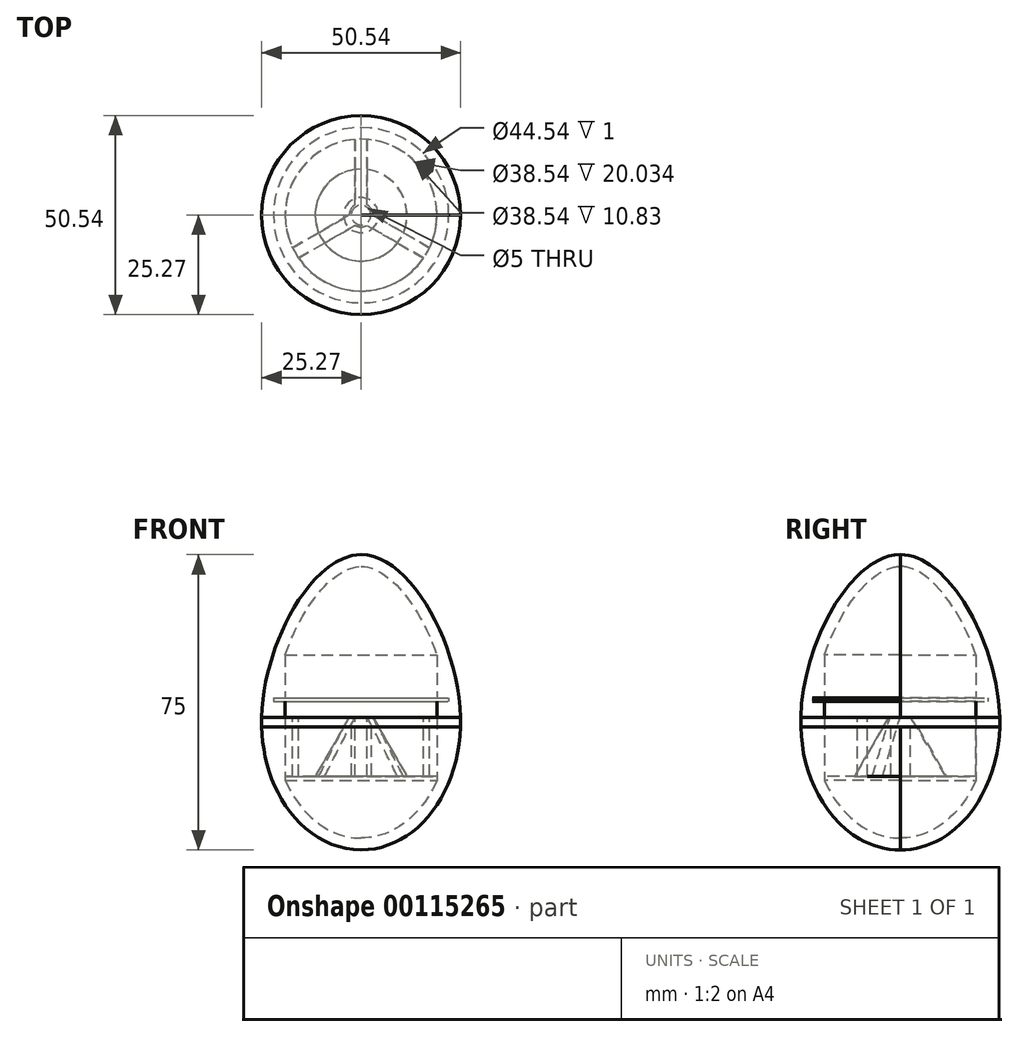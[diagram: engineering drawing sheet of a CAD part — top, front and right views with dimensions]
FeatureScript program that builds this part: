
annotation { "Feature Type Name" : "Feature", "Feature Type Description" : "" }
export const myFeature = defineFeature(function(context is Context, id is Id, definition is map)
    precondition{}
    {
        {
            var Q0;
            Q0=qCreatedBy(makeId("Front.planeOp"),FACE);
            var sketch = newSketch(context, id + "F0", { "sketchPlane" : qUnion([Q0])});
            skFitSpline(sketch, "E0", {"points": [v(0, 41.34) * mm, v(25.28, -2.21) * mm, v(0, -33.66) * mm], "startDerivative": vector(72.85, 0) * mm, "endDerivative": vector(-87.41, 0) * mm});
            skLineSegment(sketch, "E1", {"start": v(0, -33.66) * mm, "end": v(0, 41.34) * mm});
            skLineSegment(sketch, "E2", {"start": v(0, 41.34) * mm, "end": v(-30.8, 41.34) * mm, "construction": true});
            skLineSegment(sketch, "E3", {"start": v(0, -33.66) * mm, "end": v(-29.4, -33.66) * mm, "construction": true});
            skLineSegment(sketch, "E4", {"start": v(25.27, 0) * mm, "end": v(0, 0) * mm});
            skLineSegment(sketch, "E5", {"start": v(0, -33.66) * mm, "end": v(25.27, -33.66) * mm});
            skLineSegment(sketch, "E6", {"start": v(25.27, -33.66) * mm, "end": v(25.27, 41.34) * mm});
            skLineSegment(sketch, "E7", {"start": v(25.27, 41.34) * mm, "end": v(0, 41.34) * mm});
            skSolve(sketch);
        }
        {
            var Q0;
            {var subQ3=sQuery(id+"F0.wireOp",EDGE,"E4");Q0=makeQuery(id+"F0.imprint","IMPRINT",FACE,{"disambiguationData":[TD([[makeQuery(id+"F0.imprint","IMPRINT",EDGE,{"derivedFrom":subQ3}),1.0]])]});}
            var Q1;
            Q1=sQuery(id+"F0.wireOp",EDGE,"E1");
            revolve(context, id + "F1", {"entities" : qUnion([Q0]), "axis" : qUnion([Q1]), "revolveType" : RevolveType.FULL});
        }
        {
            var Q0;
            Q0=makeQuery(id+"F1.opRevolve","SWEPT_FACE",FACE,{"disambiguationData":[OSD([sQuery(id+"F0.wireOp",EDGE,"E4")])]});
            shell(context, id + "F2", {"entities" : qUnion([Q0]), "thickness" : 3 * mm});
        }
        {
            var Q0;
            {var subQ3=sQuery(id+"F0.wireOp",EDGE,"E4");Q0=makeQuery(id+"F0.imprint","IMPRINT",FACE,{"disambiguationData":[TD([[makeQuery(id+"F0.imprint","IMPRINT",EDGE,{"derivedFrom":subQ3}),-1.0]])]});}
            var Q1;
            Q1=sQuery(id+"F0.wireOp",EDGE,"E1");
            revolve(context, id + "F3", {"entities" : qUnion([Q0]), "axis" : qUnion([Q1]), "revolveType" : RevolveType.FULL});
        }
        {
            var Q0;
            Q0=makeQuery(id+"F3.opRevolve","SWEPT_FACE",FACE,{"disambiguationData":[OSD([sQuery(id+"F0.wireOp",EDGE,"E4")])]});
            var sketch = newSketch(context, id + "F4", { "sketchPlane" : qUnion([Q0])});
            skCircle(sketch, "E8", {"center": v(0, 0) * mm, "radius": 22.27 * mm});
            skCircle(sketch, "E9", {"center": v(0, 0) * mm, "radius": 19.27 * mm});
            skSolve(sketch);
        }
        {
            var Q0;
            Q0=makeQuery(id+"F3.opRevolve","SWEPT_FACE",FACE,{"disambiguationData":[OSD([sQuery(id+"F0.wireOp",EDGE,"E4")])]});
            shell(context, id + "F5", {"entities" : qUnion([Q0]), "thickness" : 3 * mm});
        }
        {
            var Q0;
            Q0=makeQuery(id+"F4.imprint","IMPRINT",FACE,{"disambiguationData":[TD([[makeQuery(id+"F4.imprint","IMPRINT",EDGE,{"derivedFrom":sQuery(id+"F4.wireOp",EDGE,"E8")}),1.0]])]});
            var Q1;
            Q1=makeQuery(id+"F4.imprint","IMPRINT",FACE,{"disambiguationData":[TD([[makeQuery(id+"F4.imprint","IMPRINT",EDGE,{"derivedFrom":sQuery(id+"F4.wireOp",EDGE,"E9")}),1.0]])]});
            extrude(context, id + "F6", {"entities" : qUnion([Q0, Q1]), "operationType" : NewBodyOperationType.REMOVE, "oppositeDirection" : true, "depth" : 5 * mm});
        }
        {
            var Q0;
            Q0=makeQuery(id+"F4.imprint","IMPRINT",FACE,{"disambiguationData":[TD([[makeQuery(id+"F4.imprint","IMPRINT",EDGE,{"derivedFrom":sQuery(id+"F4.wireOp",EDGE,"E8")}),1.0]])]});
            extrude(context, id + "F7", {"entities" : qUnion([Q0]), "operationType" : NewBodyOperationType.ADD, "oppositeDirection" : true, "depth" : 4 * mm, "hasSecondDirection" : true, "secondDirectionBound" : SecondDirectionBoundingType.UP_TO_NEXT, "secondDirectionOppositeDirection" : false, "secondDirectionDepth" : 25 * mm});
        }
        {
            var Q0;
            Q0=makeQuery(id+"F6.boolean.opBoolean","COPY",FACE,{"derivedFrom":makeQuery(id+"F6.opExtrude","CAP_FACE",FACE,{"disambiguationData":[OSD([sQuery(id+"F4.wireOp",EDGE,"E8")])],"isStart":false})});
            var sketch = newSketch(context, id + "F8", { "sketchPlane" : qUnion([Q0])});
            skPoint(sketch, "E10", {"position": v(-22.27, 0) * mm});
            skCircle(sketch, "E11", {"center": v(0, 0) * mm, "radius": 19.27 * mm});
            skSolve(sketch);
        }
        {
            var Q0;
            Q0=makeQuery(id+"F8.imprint","IMPRINT",FACE,{"disambiguationData":[TD([[makeQuery(id+"F8.imprint","IMPRINT",EDGE,{"derivedFrom":sQuery(id+"F8.wireOp",EDGE,"E11")}),-1.0]])]});
            extrude(context, id + "F9", {"entities" : qUnion([Q0]), "operationType" : NewBodyOperationType.ADD, "endBound" : BoundingType.UP_TO_NEXT, "oppositeDirection" : true, "depth" : 25 * mm});
        }
        {
            var Q0;
            Q0=qCreatedBy(makeId("Front.planeOp"),FACE);
            var sketch = newSketch(context, id + "F10", { "sketchPlane" : qUnion([Q0])});
            skLineSegment(sketch, "E12", {"start": v(3, 0) * mm, "end": v(19.27, 0) * mm});
            skLineSegment(sketch, "E13", {"start": v(19.27, 0) * mm, "end": v(19.27, -15) * mm});
            skLineSegment(sketch, "E14", {"start": v(19.27, -15) * mm, "end": v(11.66, -15) * mm});
            skLineSegment(sketch, "E15", {"start": v(11.66, -15) * mm, "end": v(3, 0) * mm});
            skLineSegment(sketch, "E16", {"start": v(4.44, -2.5) * mm, "end": v(2.5, -2.5) * mm});
            skLineSegment(sketch, "E17", {"start": v(2.5, -2.5) * mm, "end": v(2.5, -15) * mm});
            skLineSegment(sketch, "E18", {"start": v(2.5, -15) * mm, "end": v(11.66, -15) * mm});
            skLineSegment(sketch, "E19", {"start": v(0, -17.74) * mm, "end": v(0, 5.84) * mm, "construction": true});
            skSolve(sketch);
        }
        {
            var Q0;
            {var subQ2=sQuery(id+"F10.wireOp",EDGE,"E16");Q0=makeQuery(id+"F10.imprint","IMPRINT",FACE,{"disambiguationData":[TD([[makeQuery(id+"F10.imprint","IMPRINT",EDGE,{"derivedFrom":subQ2}),1.0]])]});}
            var Q1;
            Q1=sQuery(id+"F10.wireOp",EDGE,"E19");
            revolve(context, id + "F11", {"entities" : qUnion([Q0]), "axis" : qUnion([Q1]), "revolveType" : RevolveType.FULL});
        }
        {
            var Q0;
            {var subQ3=sQuery(id+"F10.wireOp",EDGE,"E12");Q0=makeQuery(id+"F10.imprint","IMPRINT",FACE,{"disambiguationData":[TD([[makeQuery(id+"F10.imprint","IMPRINT",EDGE,{"derivedFrom":subQ3}),-1.0]])]});}
            var Q1;
            Q1=sQuery(id+"F10.wireOp",EDGE,"E19");
            revolve(context, id + "F12", {"entities" : qUnion([Q0]), "axis" : qUnion([Q1]), "revolveType" : RevolveType.FULL});
        }
        {
            var Q0;
            Q0=makeQuery(id+"F12.opRevolve","SWEPT_FACE",FACE,{"disambiguationData":[OSD([sQuery(id+"F10.wireOp",EDGE,"E12")])]});
            var sketch = newSketch(context, id + "F13", { "sketchPlane" : qUnion([Q0])});
            skLineSegment(sketch, "E20", {"start": v(1.5, 2.6) * mm, "end": v(1.5, 19.21) * mm});
            skLineSegment(sketch, "E21", {"start": v(0, 0) * mm, "end": v(0, 19.27) * mm, "construction": true});
            skLineSegment(sketch, "E22.MirrorCS", {"start": v(-1.5, 2.6) * mm, "end": v(-1.5, 19.21) * mm});
            skArc(sketch, "E23", {"start": v(-1.5, 19.21) * mm, "mid": v(0, 19.27) * mm, "end": v(1.5, 19.21) * mm});
            skArc(sketch, "E24", {"start": v(-1.5, 2.6) * mm, "mid": v(0, 3) * mm, "end": v(1.5, 2.6) * mm});
            skArc(sketch, "E25.1.0", {"start": v(-1.5, -2.6) * mm, "mid": v(-2.6, -1.5) * mm, "end": v(-3, 0) * mm});
            skLineSegment(sketch, "E25.1.1", {"start": v(-1.5, -2.6) * mm, "end": v(-15.89, -10.9) * mm});
            skLineSegment(sketch, "E25.1.2", {"start": v(-3, 0) * mm, "end": v(-17.39, -8.3) * mm});
            skArc(sketch, "E25.1.3", {"start": v(-15.89, -10.9) * mm, "mid": v(-16.69, -9.64) * mm, "end": v(-17.39, -8.3) * mm});
            skArc(sketch, "E25.2.0", {"start": v(3, 0) * mm, "mid": v(2.6, -1.5) * mm, "end": v(1.5, -2.6) * mm});
            skLineSegment(sketch, "E25.2.1", {"start": v(3, 0) * mm, "end": v(17.39, -8.3) * mm});
            skLineSegment(sketch, "E25.2.2", {"start": v(1.5, -2.6) * mm, "end": v(15.89, -10.9) * mm});
            skArc(sketch, "E25.2.3", {"start": v(17.39, -8.3) * mm, "mid": v(16.69, -9.64) * mm, "end": v(15.89, -10.9) * mm});
            skSolve(sketch);
        }
        {
            var Q0;
            Q0=qSketchRegion(id+"F13",true);
            extrude(context, id + "F14", {"entities" : qUnion([Q0]), "operationType" : NewBodyOperationType.REMOVE, "endBound" : BoundingType.UP_TO_NEXT, "oppositeDirection" : true, "depth" : 25 * mm});
        }
    });
